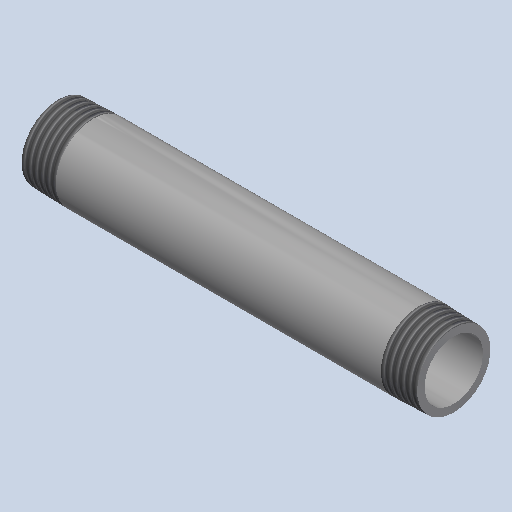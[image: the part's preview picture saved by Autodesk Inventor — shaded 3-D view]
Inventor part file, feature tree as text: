
AUTODESK INVENTOR PART (.ipt)
format: ipt  version: 2025 (Build 290162000, 162)  size: 195,584 bytes
history: native  units: mm (DEFAULTED — no unit token found)
features: other x8, revolve x1
ambient origin geometry x8: Origin, YZ Plane, XZ Plane, XY Plane, X Axis, Y Axis, Z Axis, Center Point
bodies: Solid1 (feature_tree)
feature tree (9):
  revolve  "Revolution1"  [1 undecoded]
  other  "Work Axis1"
  other  "Work Point5"
  other  "Work Axis2"
  other  "Work Point6"
  other  "Work Axis3"
  other  "Work Axis4"
  other  "Work Point7"
  other  "Work Point8"
note: 1 required parameter value undecoded (feature->parameter linkage not recoverable at this tier; creation-order binding heuristic only, values carry confidence <= 0.55)
